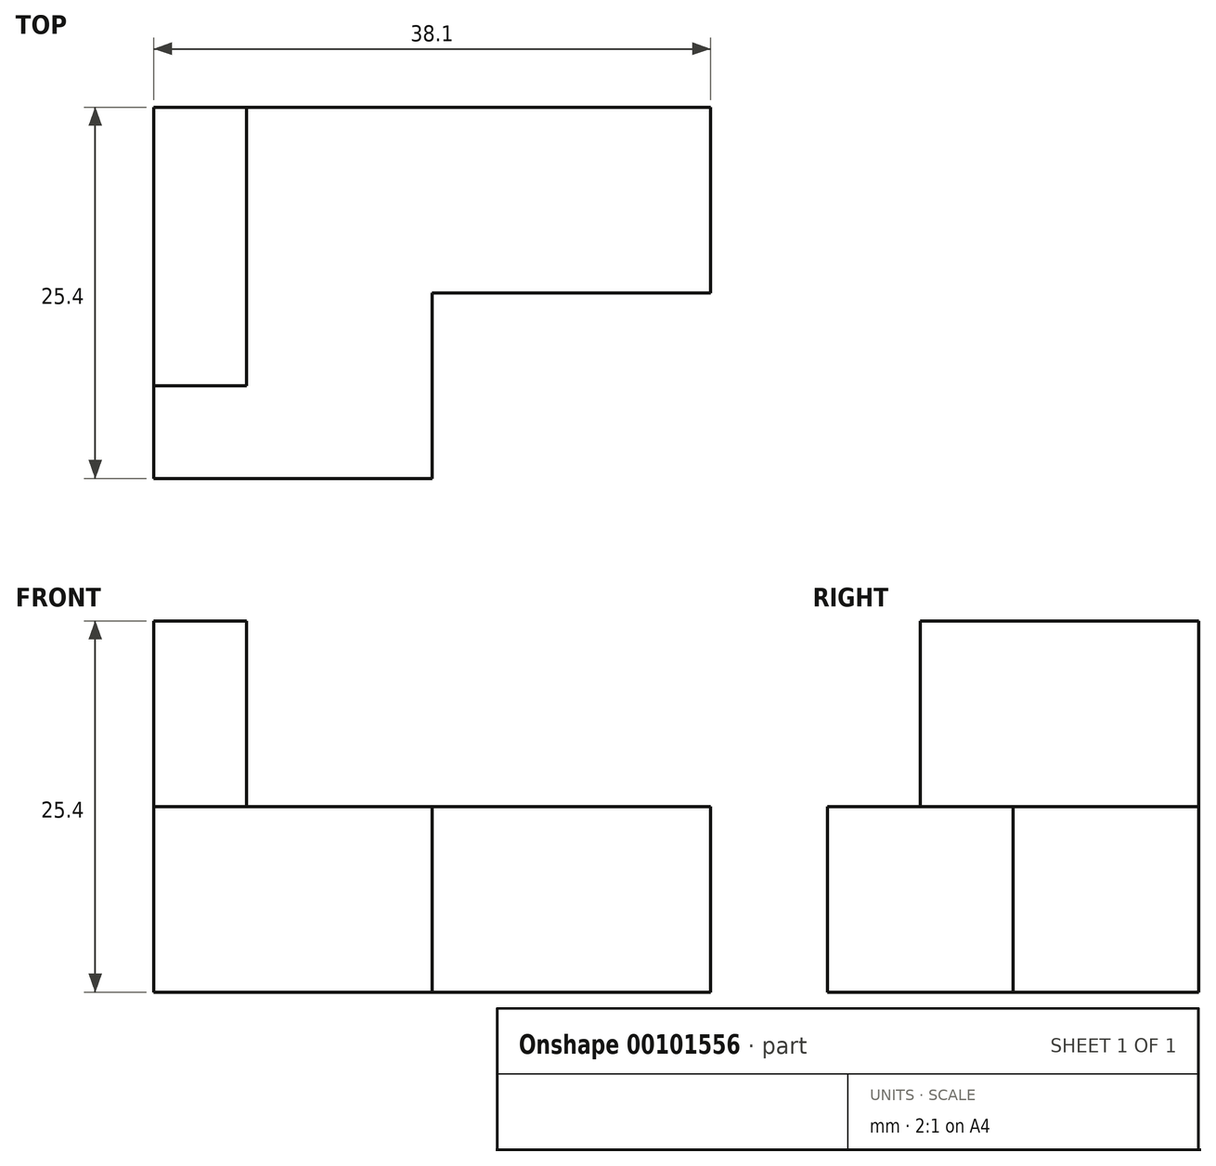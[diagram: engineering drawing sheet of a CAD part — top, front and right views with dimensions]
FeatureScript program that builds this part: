
annotation { "Feature Type Name" : "Feature", "Feature Type Description" : "" }
export const myFeature = defineFeature(function(context is Context, id is Id, definition is map)
    precondition{}
    {
        {
            var Q0;
            Q0=qCreatedBy(makeId("Top.planeOp"),FACE);
            var sketch = newSketch(context, id + "F0", { "sketchPlane" : qUnion([Q0])});
            skLineSegment(sketch, "E0", {"start": v(0, -25.4) * mm, "end": v(0, 0) * mm});
            skLineSegment(sketch, "E1", {"start": v(0, 0) * mm, "end": v(38.1, 0) * mm});
            skLineSegment(sketch, "E2", {"start": v(38.1, 0) * mm, "end": v(38.1, -12.7) * mm});
            skLineSegment(sketch, "E3", {"start": v(38.1, -12.7) * mm, "end": v(19.05, -12.7) * mm});
            skLineSegment(sketch, "E4", {"start": v(19.05, -12.7) * mm, "end": v(19.05, -25.4) * mm});
            skLineSegment(sketch, "E5", {"start": v(19.05, -25.4) * mm, "end": v(0, -25.4) * mm});
            skSolve(sketch);
        }
        {
            var Q0;
            Q0=qCreatedBy(makeId("Front.planeOp"),FACE);
            var sketch = newSketch(context, id + "F1", { "sketchPlane" : qUnion([Q0])});
            skLineSegment(sketch, "E6", {"start": v(0, 0) * mm, "end": v(0, 25.4) * mm});
            skLineSegment(sketch, "E7", {"start": v(0, 25.4) * mm, "end": v(6.35, 25.4) * mm});
            skLineSegment(sketch, "E8", {"start": v(6.35, 25.4) * mm, "end": v(6.35, 0) * mm});
            skLineSegment(sketch, "E9", {"start": v(6.35, 0) * mm, "end": v(0, 0) * mm});
            skSolve(sketch);
        }
        {
            var Q0;
            Q0=makeQuery(id+"F0.imprint","IMPRINT",FACE,{"disambiguationData":[TD([[makeQuery(id+"F0.imprint","IMPRINT",EDGE,{"derivedFrom":sQuery(id+"F0.wireOp",EDGE,"E0")}),-1.0]])]});
            extrude(context, id + "F2", {"entities" : qUnion([Q0]), "depth" : 12.7 * mm});
        }
        {
            var Q0;
            Q0 = qSketchRegion(id + "F1", true);
            extrude(context, id + "F3", {"entities" : qUnion([Q0]), "operationType" : NewBodyOperationType.ADD, "depth" : 19.05 * mm});
        }
    });
